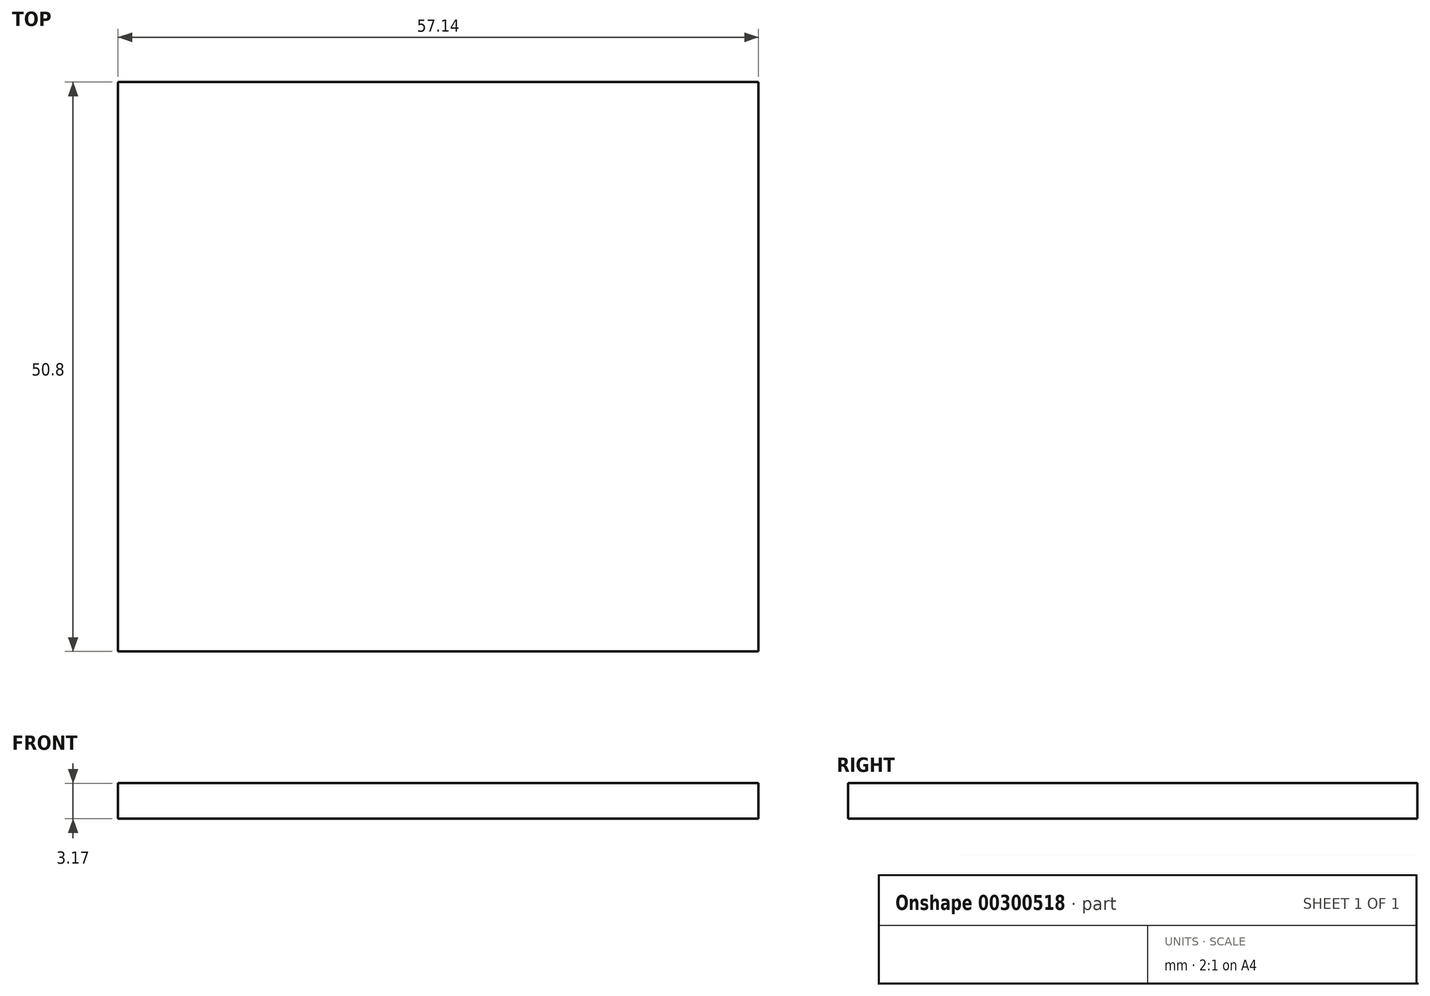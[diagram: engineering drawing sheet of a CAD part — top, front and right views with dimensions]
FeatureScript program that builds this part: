
annotation { "Feature Type Name" : "Feature", "Feature Type Description" : "" }
export const myFeature = defineFeature(function(context is Context, id is Id, definition is map)
    precondition{}
    {
        {
            var Q0;
            Q0=qCreatedBy(makeId("Top.planeOp"),FACE);
            var sketch = newSketch(context, id + "F0", { "sketchPlane" : qUnion([Q0])});
            skLineSegment(sketch, "E0.bottom", {"start": v(-28.57, 25.4) * mm, "end": v(28.58, 25.4) * mm});
            skLineSegment(sketch, "E0.top", {"start": v(-28.57, -25.4) * mm, "end": v(28.57, -25.4) * mm});
            skLineSegment(sketch, "E0.left", {"start": v(-28.57, 25.4) * mm, "end": v(-28.58, -25.4) * mm});
            skLineSegment(sketch, "E0.right", {"start": v(28.58, 25.4) * mm, "end": v(28.57, -25.4) * mm});
            skPoint(sketch, "E0.middle", {"position": v(0, 0) * mm});
            skSolve(sketch);
        }
        {
            var Q0;
            Q0 = qSketchRegion(id + "F0", true);
            extrude(context, id + "F1", {"entities" : qUnion([Q0]), "depth" : 3.17 * mm});
        }
    });
